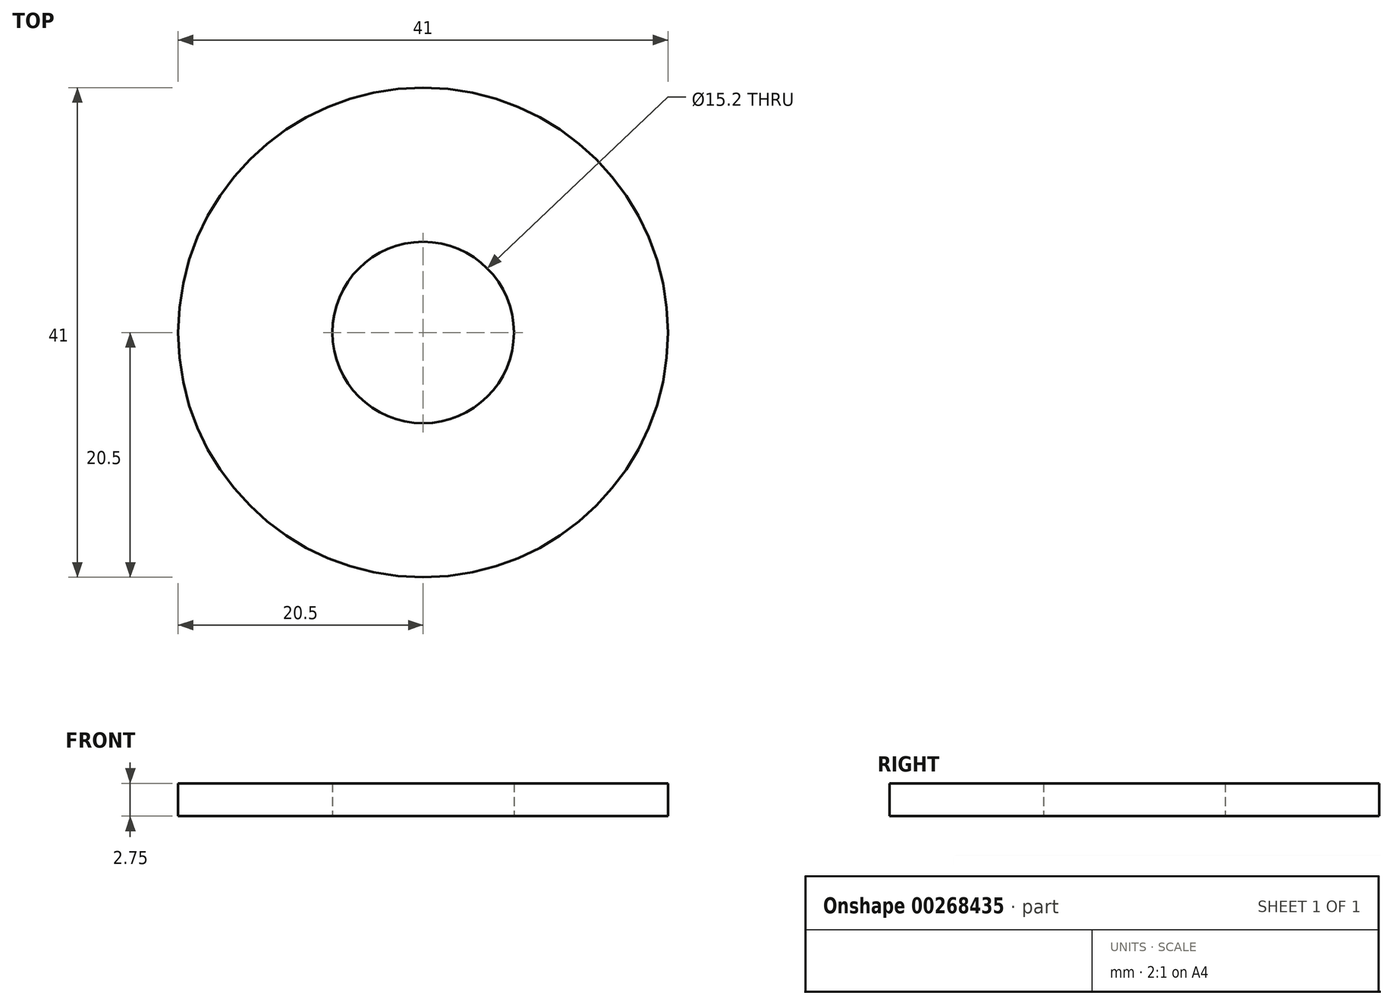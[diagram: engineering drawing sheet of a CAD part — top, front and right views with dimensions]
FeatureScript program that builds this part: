
annotation { "Feature Type Name" : "Feature", "Feature Type Description" : "" }
export const myFeature = defineFeature(function(context is Context, id is Id, definition is map)
    precondition{}
    {
        {
            var Q0;
            Q0=qCreatedBy(makeId("Top.planeOp"),FACE);
            var sketch = newSketch(context, id + "F0", { "sketchPlane" : qUnion([Q0])});
            skCircle(sketch, "E0", {"center": v(0, 0) * mm, "radius": 20.5 * mm});
            skCircle(sketch, "E1", {"center": v(0, 0) * mm, "radius": 7.6 * mm});
            skSolve(sketch);
        }
        {
            var Q0;
            Q0=makeQuery(id+"F0.imprint","IMPRINT",FACE,{"disambiguationData":[TD([[makeQuery(id+"F0.imprint","IMPRINT",EDGE,{"derivedFrom":sQuery(id+"F0.wireOp",EDGE,"E0")}),1.0]])]});
            extrude(context, id + "F1", {"entities" : qUnion([Q0]), "depth" : 2.75 * mm});
        }
    });
